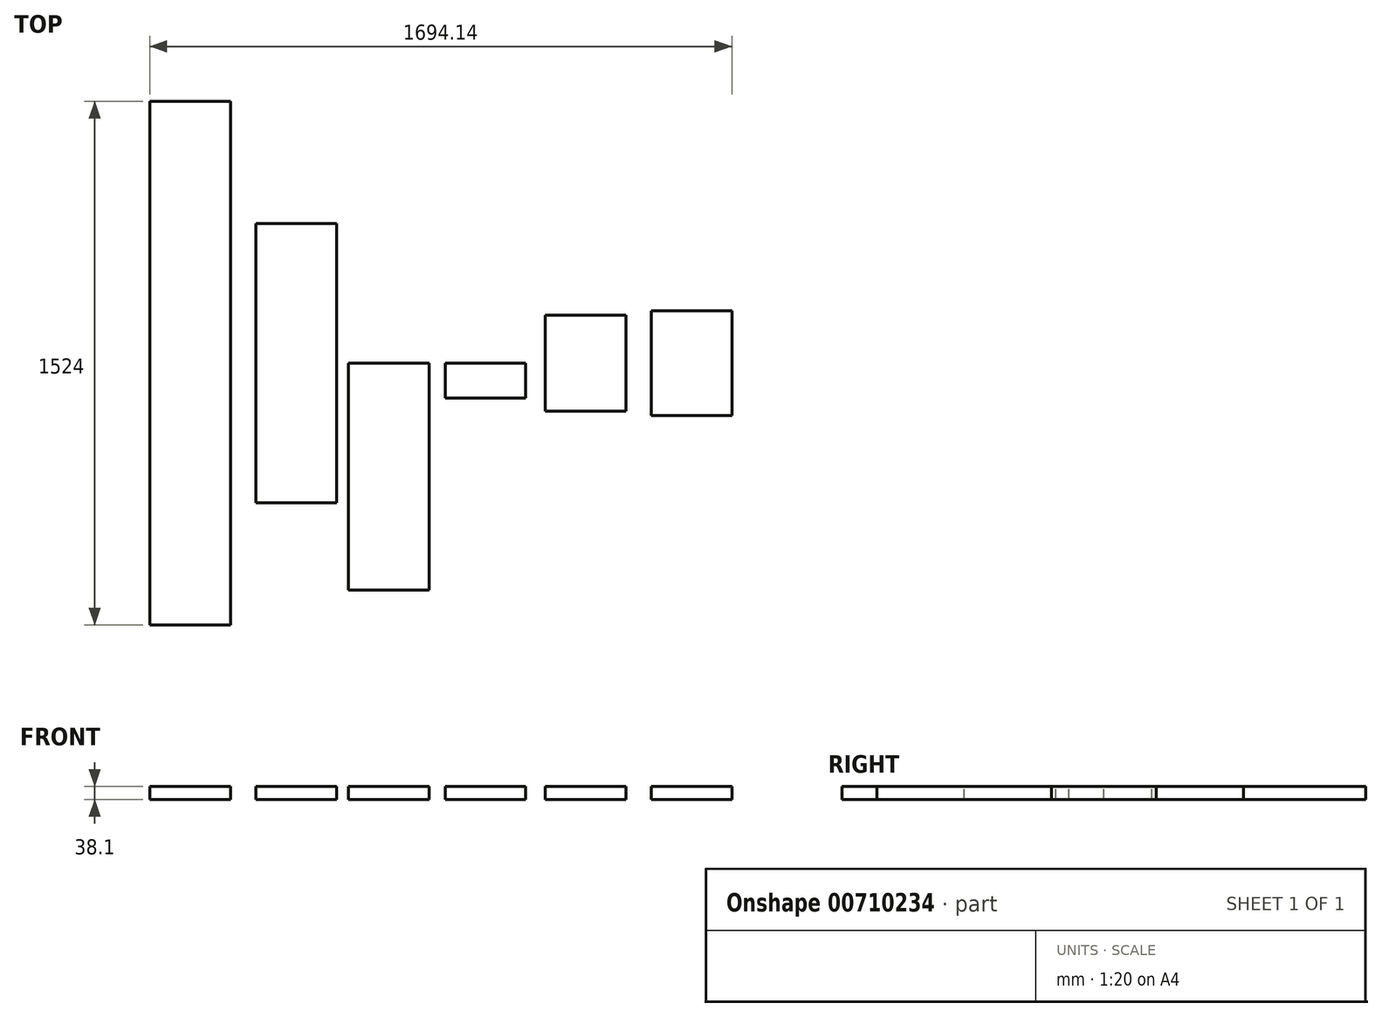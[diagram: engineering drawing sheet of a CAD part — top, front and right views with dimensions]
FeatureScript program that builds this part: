
annotation { "Feature Type Name" : "Feature", "Feature Type Description" : "" }
export const myFeature = defineFeature(function(context is Context, id is Id, definition is map)
    precondition{}
    {
        {
            var Q0;
            Q0=qCreatedBy(makeId("Front.planeOp"),FACE);
            var sketch = newSketch(context, id + "F0", { "sketchPlane" : qUnion([Q0])});
            skLineSegment(sketch, "E0.bottom", {"start": v(117.48, -19.05) * mm, "end": v(-117.48, -19.05) * mm});
            skLineSegment(sketch, "E0.top", {"start": v(117.48, 19.05) * mm, "end": v(-117.48, 19.05) * mm});
            skLineSegment(sketch, "E0.left", {"start": v(117.48, -19.05) * mm, "end": v(117.48, 19.05) * mm});
            skLineSegment(sketch, "E0.right", {"start": v(-117.48, -19.05) * mm, "end": v(-117.48, 19.05) * mm});
            skPoint(sketch, "E0.middle", {"position": v(0, 0) * mm});
            skSolve(sketch);
        }
        {
            var Q0;
            Q0=qSketchRegion(id+"F0",true);
            extrude(context, id + "F1", {"entities" : qUnion([Q0]), "endBound" : BoundingType.SYMMETRIC, "depth" : 1524 * mm, "offsetDistance" : 25 * mm});
        }
        {
            var Q0;
            Q0=qCreatedBy(makeId("Front.planeOp"),FACE);
            var sketch = newSketch(context, id + "F2", { "sketchPlane" : qUnion([Q0])});
            skLineSegment(sketch, "E1.bottom", {"start": v(426.44, -19.05) * mm, "end": v(191.49, -19.05) * mm});
            skLineSegment(sketch, "E1.top", {"start": v(426.44, 19.05) * mm, "end": v(191.49, 19.05) * mm});
            skLineSegment(sketch, "E1.left", {"start": v(426.44, -19.05) * mm, "end": v(426.44, 19.05) * mm});
            skLineSegment(sketch, "E1.right", {"start": v(191.49, -19.05) * mm, "end": v(191.49, 19.05) * mm});
            skPoint(sketch, "E1.middle", {"position": v(308.96, 0) * mm});
            skSolve(sketch);
        }
        {
            var Q0;
            Q0=qSketchRegion(id+"F2",true);
            extrude(context, id + "F3", {"entities" : qUnion([Q0]), "endBound" : BoundingType.SYMMETRIC, "depth" : 812.8 * mm, "offsetDistance" : 25 * mm});
        }
        {
            var Q0;
            Q0=qCreatedBy(makeId("Front.planeOp"),FACE);
            var sketch = newSketch(context, id + "F4", { "sketchPlane" : qUnion([Q0])});
            skLineSegment(sketch, "E2.bottom", {"start": v(695.48, -19.05) * mm, "end": v(460.53, -19.05) * mm});
            skLineSegment(sketch, "E2.top", {"start": v(695.48, 19.05) * mm, "end": v(460.53, 19.05) * mm});
            skLineSegment(sketch, "E2.left", {"start": v(695.48, -19.05) * mm, "end": v(695.48, 19.05) * mm});
            skLineSegment(sketch, "E2.right", {"start": v(460.53, -19.05) * mm, "end": v(460.53, 19.05) * mm});
            skPoint(sketch, "E2.middle", {"position": v(578, 0) * mm});
            skSolve(sketch);
        }
        {
            var Q0;
            Q0=qSketchRegion(id+"F4",true);
            extrude(context, id + "F5", {"entities" : qUnion([Q0]), "depth" : 660.4 * mm, "offsetDistance" : 25 * mm});
        }
        {
            var Q0;
            Q0=qCreatedBy(makeId("Front.planeOp"),FACE);
            var sketch = newSketch(context, id + "F6", { "sketchPlane" : qUnion([Q0])});
            skLineSegment(sketch, "E3.bottom", {"start": v(977.1, -19.05) * mm, "end": v(742.15, -19.05) * mm});
            skLineSegment(sketch, "E3.top", {"start": v(977.1, 19.05) * mm, "end": v(742.15, 19.05) * mm});
            skLineSegment(sketch, "E3.left", {"start": v(977.1, -19.05) * mm, "end": v(977.1, 19.05) * mm});
            skLineSegment(sketch, "E3.right", {"start": v(742.15, -19.05) * mm, "end": v(742.15, 19.05) * mm});
            skPoint(sketch, "E3.middle", {"position": v(859.62, 0) * mm});
            skSolve(sketch);
        }
        {
            var Q0;
            Q0=qSketchRegion(id+"F6",true);
            extrude(context, id + "F7", {"entities" : qUnion([Q0]), "depth" : 101.6 * mm, "offsetDistance" : 25 * mm});
        }
        {
            var Q0;
            Q0=qCreatedBy(makeId("Front.planeOp"),FACE);
            var sketch = newSketch(context, id + "F8", { "sketchPlane" : qUnion([Q0])});
            skLineSegment(sketch, "E4.bottom", {"start": v(1268.86, -19.05) * mm, "end": v(1033.91, -19.05) * mm});
            skLineSegment(sketch, "E4.top", {"start": v(1268.86, 19.05) * mm, "end": v(1033.91, 19.05) * mm});
            skLineSegment(sketch, "E4.left", {"start": v(1268.86, -19.05) * mm, "end": v(1268.86, 19.05) * mm});
            skLineSegment(sketch, "E4.right", {"start": v(1033.91, -19.05) * mm, "end": v(1033.91, 19.05) * mm});
            skPoint(sketch, "E4.middle", {"position": v(1151.39, 0) * mm});
            skSolve(sketch);
        }
        {
            var Q0;
            Q0=qSketchRegion(id+"F8",true);
            extrude(context, id + "F9", {"entities" : qUnion([Q0]), "endBound" : BoundingType.SYMMETRIC, "depth" : 279.4 * mm, "offsetDistance" : 25 * mm});
        }
        {
            var Q0;
            Q0=qCreatedBy(makeId("Front.planeOp"),FACE);
            var sketch = newSketch(context, id + "F10", { "sketchPlane" : qUnion([Q0])});
            skLineSegment(sketch, "E5.bottom", {"start": v(1576.67, -19.05) * mm, "end": v(1341.72, -19.05) * mm});
            skLineSegment(sketch, "E5.top", {"start": v(1576.67, 19.05) * mm, "end": v(1341.72, 19.05) * mm});
            skLineSegment(sketch, "E5.left", {"start": v(1576.67, -19.05) * mm, "end": v(1576.67, 19.05) * mm});
            skLineSegment(sketch, "E5.right", {"start": v(1341.72, -19.05) * mm, "end": v(1341.72, 19.05) * mm});
            skPoint(sketch, "E5.middle", {"position": v(1459.2, 0) * mm});
            skSolve(sketch);
        }
        {
            var Q0;
            Q0=qSketchRegion(id+"F10",true);
            extrude(context, id + "F11", {"entities" : qUnion([Q0]), "endBound" : BoundingType.SYMMETRIC, "depth" : 304.8 * mm, "offsetDistance" : 25 * mm});
        }
    });
